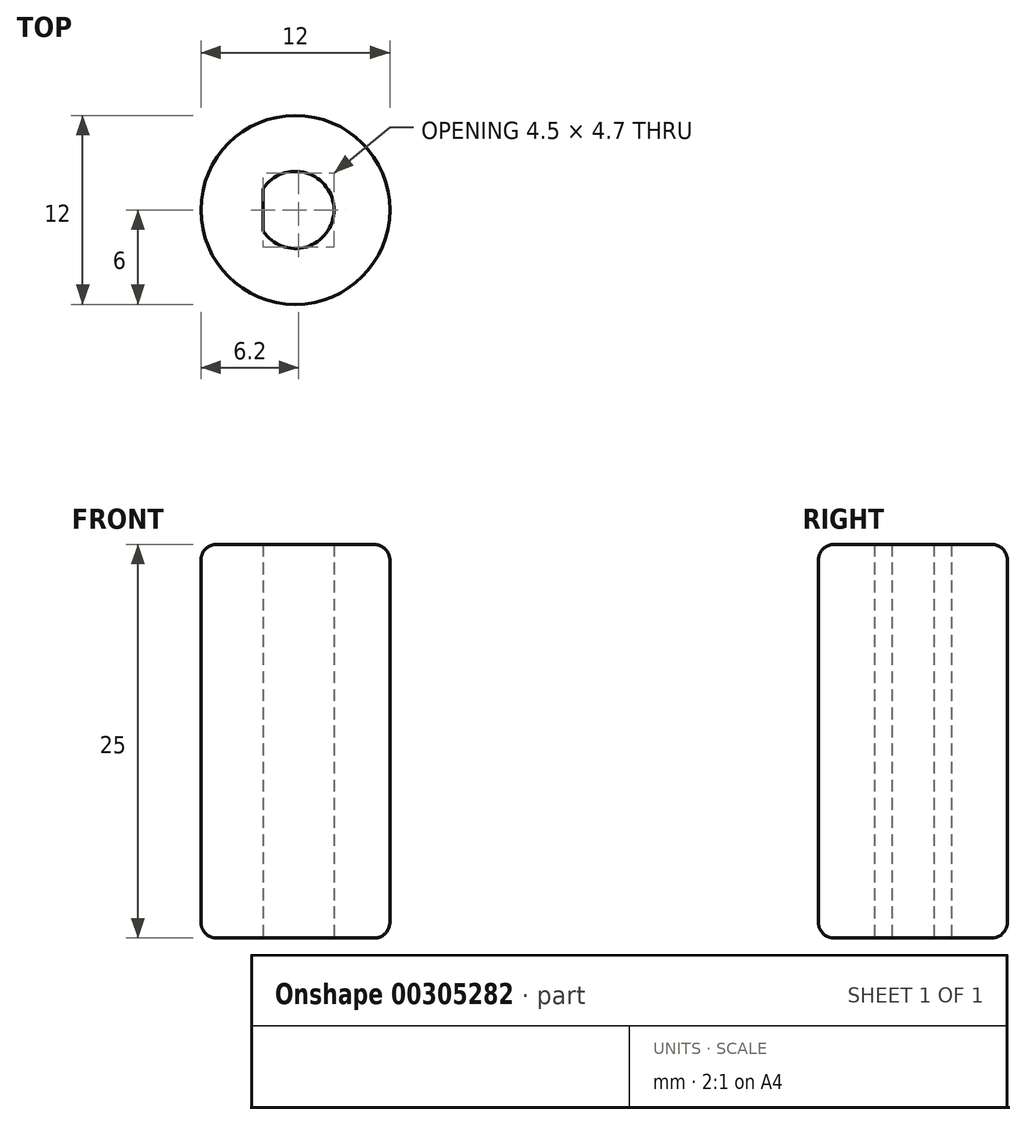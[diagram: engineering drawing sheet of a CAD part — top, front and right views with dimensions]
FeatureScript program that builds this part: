
annotation { "Feature Type Name" : "Feature", "Feature Type Description" : "" }
export const myFeature = defineFeature(function(context is Context, id is Id, definition is map)
    precondition{}
    {
        {
            var Q0;
            Q0=qCreatedBy(makeId("Top.planeOp"),FACE);
            var sketch = newSketch(context, id + "F0", { "sketchPlane" : qUnion([Q0])});
            skCircle(sketch, "E0", {"center": v(0, 0) * mm, "radius": 6 * mm});
            skSolve(sketch);
        }
        {
            var Q0;
            Q0=qCreatedBy(makeId("Top.planeOp"),FACE);
            var sketch = newSketch(context, id + "F1", { "sketchPlane" : qUnion([Q0])});
            skArc(sketch, "E1", {"start": v(-2.05, -1.34) * mm, "mid": v(2.45, 0) * mm, "end": v(-2.05, 1.34) * mm});
            skLineSegment(sketch, "E2", {"start": v(-2.05, -1.34) * mm, "end": v(-2.05, 1.34) * mm});
            skSolve(sketch);
        }
        {
            var Q0;
            Q0=makeQuery(id+"F0.imprint","IMPRINT",FACE,{"disambiguationData":[TD([[makeQuery(id+"F0.imprint","IMPRINT",EDGE,{"derivedFrom":sQuery(id+"F0.wireOp",EDGE,"E0")}),1.0]])]});
            extrude(context, id + "F2", {"entities" : qUnion([Q0]), "depth" : 25 * mm});
        }
        {
            var Q0;
            Q0=makeQuery(id+"F1.imprint","IMPRINT",FACE,{"disambiguationData":[TD([[makeQuery(id+"F1.imprint","IMPRINT",EDGE,{"derivedFrom":sQuery(id+"F1.wireOp",EDGE,"E1")}),1.0]])]});
            extrude(context, id + "F3", {"entities" : qUnion([Q0]), "operationType" : NewBodyOperationType.REMOVE, "depth" : 25 * mm});
        }
        {
            var Q0;
            Q0=makeQuery(id+"F2.opExtrude","CAP_EDGE",EDGE,{"disambiguationData":[OSD([sQuery(id+"F0.wireOp",EDGE,"E0")])],"isStart":false});
            var Q1;
            Q1=makeQuery(id+"F2.opExtrude","CAP_EDGE",EDGE,{"disambiguationData":[OSD([sQuery(id+"F0.wireOp",EDGE,"E0")])],"isStart":true});
            fillet(context, id + "F4", {"entities" : qUnion([Q0, Q1]), "radius" : 1 * mm, "tangentPropagation" : true, "allowEdgeOverflow" : false});
        }
    });
